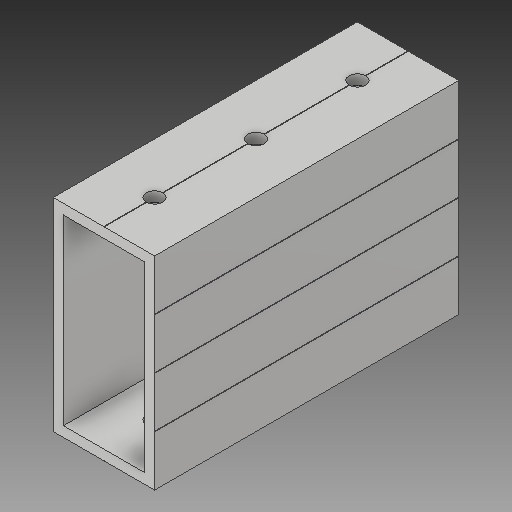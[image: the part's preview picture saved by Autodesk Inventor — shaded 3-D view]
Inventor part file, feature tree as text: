
AUTODESK INVENTOR PART (.ipt)
format: ipt  version: 2017 (Build 210142000, 142)  size: 449,536 bytes
history: native  units: in
note: dims shown in document units (in); Inventor stores cm internally (conversion verified against a paired STEP export)
features: reference x4, other x4, sketch x2, extrude x2, plane x1
ambient origin geometry x8: Origin, YZ Plane, XZ Plane, XY Plane, X Axis, Y Axis, Z Axis, Center Point
bodies: Solid1 (feature_tree)
feature tree (13):
  sketch  "Sketch1"  dims[d0=3.0in d3=3.0in d4=0.94in d12=0.94in d13=3.0in]
  extrude  "Extrusion2"  Depth=3.0in
  extrude  "Extrusion3"  Depth=1.0in TaperAngle=0.0deg
  plane  "Work Plane4"
  sketch  "Sketch2"  dims[d30=1.0in d31=0.0in d32=1.0in d33=0.0in d21=1.0in d22=1.0in]
  reference  "Reference1"
  reference  "Reference2"
  reference  "Reference3"
  reference  "Reference4"
  other  "Cut-Extrude2"
  other  "<userpath>\Documents\GitHub\2898-STEAMworks-CAD\2898-17-A-0100\SideFrame.iam"
  other  "SideFrame.iam"
  other  "WCP_DS_Gearbox:1"
